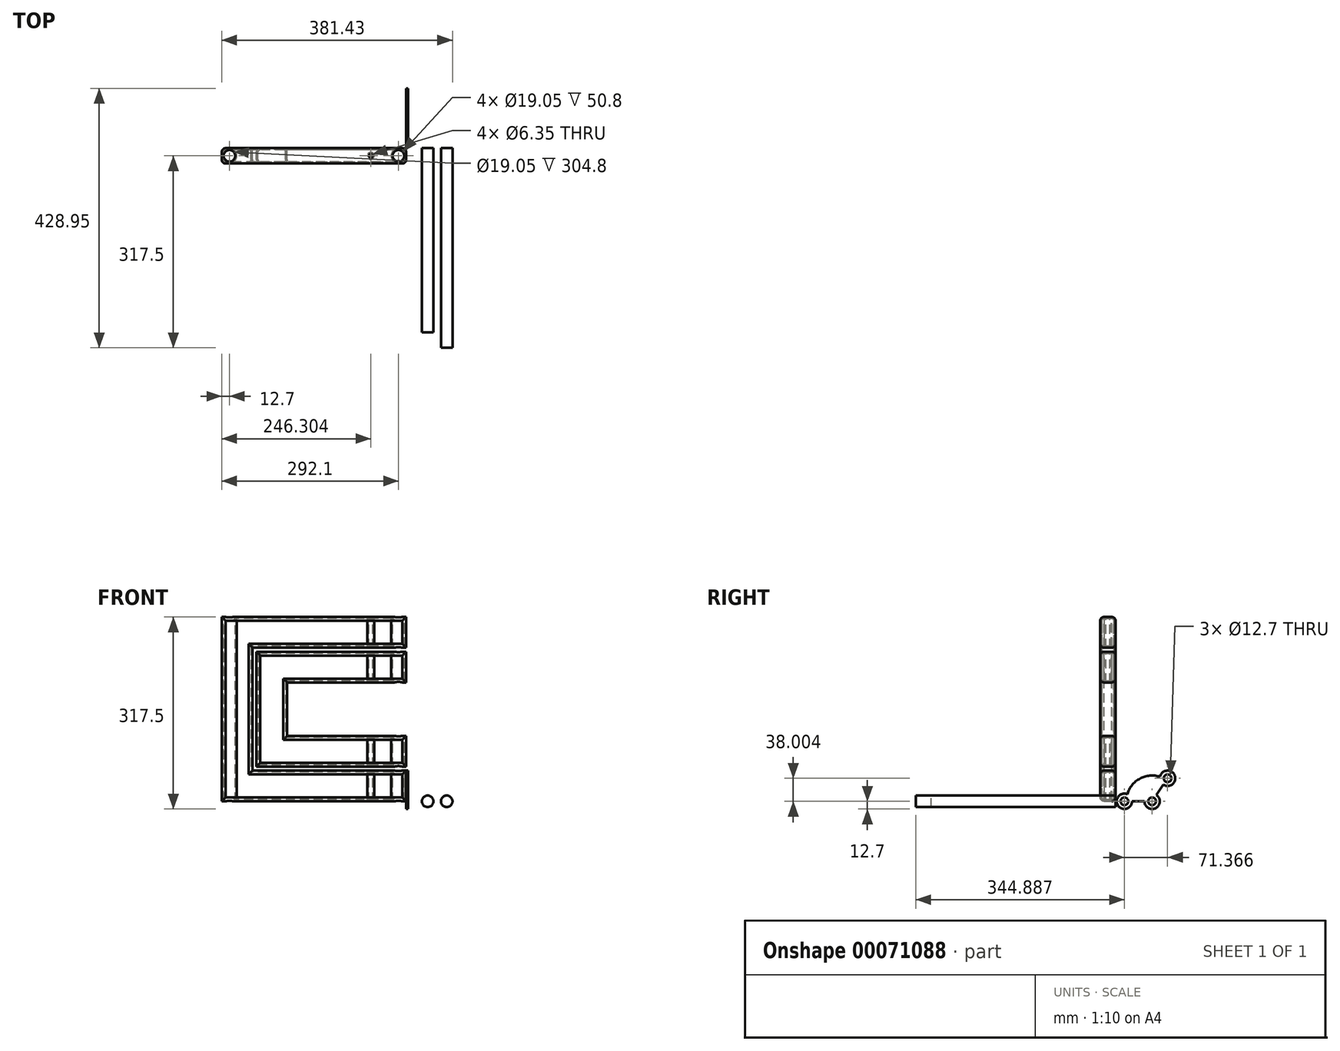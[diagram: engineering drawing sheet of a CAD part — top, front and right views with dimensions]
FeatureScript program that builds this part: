
annotation { "Feature Type Name" : "Feature", "Feature Type Description" : "" }
export const myFeature = defineFeature(function(context is Context, id is Id, definition is map)
    precondition{}
    {
        {
            var Q0;
            Q0=qCreatedBy(makeId("Front.planeOp"),FACE);
            var sketch = newSketch(context, id + "F0", { "sketchPlane" : qUnion([Q0])});
            skLineSegment(sketch, "E0.bottom", {"start": v(0, 0) * mm, "end": v(-304.8, 0) * mm});
            skLineSegment(sketch, "E0.top", {"start": v(0, 304.8) * mm, "end": v(-304.8, 304.8) * mm});
            skLineSegment(sketch, "E0.left", {"start": v(0, 0) * mm, "end": v(0, 304.8) * mm});
            skLineSegment(sketch, "E0.right", {"start": v(-304.8, 0) * mm, "end": v(-304.8, 304.8) * mm});
            skLineSegment(sketch, "E1.bottom", {"start": v(0, 254) * mm, "end": v(-254, 254) * mm});
            skLineSegment(sketch, "E1.top", {"start": v(0, 50.8) * mm, "end": v(-254, 50.8) * mm});
            skLineSegment(sketch, "E1.left", {"start": v(0, 254) * mm, "end": v(0, 50.8) * mm});
            skLineSegment(sketch, "E1.right", {"start": v(-254, 254) * mm, "end": v(-254, 50.8) * mm});
            skLineSegment(sketch, "E2.bottom", {"start": v(-253.75, 253.75) * mm, "end": v(0, 253.75) * mm});
            skLineSegment(sketch, "E2.top", {"start": v(-253.75, 51.05) * mm, "end": v(0, 51.05) * mm});
            skLineSegment(sketch, "E2.left", {"start": v(-253.75, 253.75) * mm, "end": v(-253.75, 51.05) * mm});
            skLineSegment(sketch, "E2.right", {"start": v(0, 253.75) * mm, "end": v(0, 51.05) * mm});
            skLineSegment(sketch, "E3.bottom", {"start": v(0, 196.6) * mm, "end": v(-196.6, 196.6) * mm});
            skLineSegment(sketch, "E3.top", {"start": v(0, 108.2) * mm, "end": v(-196.6, 108.2) * mm});
            skLineSegment(sketch, "E3.left", {"start": v(0, 196.6) * mm, "end": v(0, 108.2) * mm});
            skLineSegment(sketch, "E3.right", {"start": v(-196.6, 196.6) * mm, "end": v(-196.6, 108.2) * mm});
            skLineSegment(sketch, "E4.bottom", {"start": v(0, 247.4) * mm, "end": v(-247.4, 247.4) * mm});
            skLineSegment(sketch, "E4.top", {"start": v(0, 57.4) * mm, "end": v(-247.4, 57.4) * mm});
            skLineSegment(sketch, "E4.left", {"start": v(0, 247.4) * mm, "end": v(0, 57.4) * mm});
            skLineSegment(sketch, "E4.right", {"start": v(-247.4, 247.4) * mm, "end": v(-247.4, 57.4) * mm});
            skSolve(sketch);
        }
        {
            var Q0;
            {var subQ4=sQuery(id+"F0.wireOp",EDGE,"E0.bottom");Q0=makeQuery(id+"F0.imprint","IMPRINT",FACE,{"disambiguationData":[TD([[makeQuery(id+"F0.imprint","IMPRINT",EDGE,{"derivedFrom":subQ4}),-1.0]])]});}
            var Q1;
            {var subQ2=sQuery(id+"F0.wireOp",EDGE,"E3.bottom");Q1=makeQuery(id+"F0.imprint","IMPRINT",FACE,{"disambiguationData":[TD([[makeQuery(id+"F0.imprint","IMPRINT",EDGE,{"derivedFrom":subQ2}),-1.0]])]});}
            extrude(context, id + "F1", {"entities" : qUnion([Q0, Q1]), "depth" : 25.4 * mm});
        }
        {
            var Q0;
            Q0=makeQuery(id+"F1.opExtrude","SWEPT_FACE",FACE,{"disambiguationData":[OSD([sQuery(id+"F0.wireOp",EDGE,"E0.top")])]});
            var sketch = newSketch(context, id + "F2", { "sketchPlane" : qUnion([Q0])});
            skLineSegment(sketch, "E5.0", {"start": v(0, 0) * mm, "end": v(-304.8, 0) * mm});
            skLineSegment(sketch, "E5.1", {"start": v(-304.8, -25.4) * mm, "end": v(-304.8, 0) * mm});
            skLineSegment(sketch, "E5.2", {"start": v(0, -25.4) * mm, "end": v(-304.8, -25.4) * mm});
            skLineSegment(sketch, "E5.3", {"start": v(0, -25.4) * mm, "end": v(0, 0) * mm});
            skCircle(sketch, "E6", {"center": v(-292.1, -12.7) * mm, "radius": 9.53 * mm});
            skCircle(sketch, "E7", {"center": v(-12.7, -12.7) * mm, "radius": 9.53 * mm});
            skCircle(sketch, "E8", {"center": v(-241.3, -12.7) * mm, "radius": 9.53 * mm});
            skSolve(sketch);
        }
        {
            var Q0;
            Q0=makeQuery(id+"F2.imprint","IMPRINT",FACE,{"disambiguationData":[TD([[makeQuery(id+"F2.imprint","IMPRINT",EDGE,{"derivedFrom":sQuery(id+"F2.wireOp",EDGE,"E6")}),1.0]])]});
            var Q1;
            Q1=makeQuery(id+"F2.imprint","IMPRINT",FACE,{"disambiguationData":[TD([[makeQuery(id+"F2.imprint","IMPRINT",EDGE,{"derivedFrom":sQuery(id+"F2.wireOp",EDGE,"E7")}),1.0]])]});
            extrude(context, id + "F3", {"entities" : qUnion([Q0, Q1]), "operationType" : NewBodyOperationType.REMOVE, "endBound" : BoundingType.THROUGH_ALL, "oppositeDirection" : true, "depth" : 25.4 * mm});
        }
        {
            var Q0;
            Q0=qCreatedBy(makeId("Front.planeOp"),FACE);
            var sketch = newSketch(context, id + "F4", { "sketchPlane" : qUnion([Q0])});
            skCircle(sketch, "E9", {"center": v(67.1, 0) * mm, "radius": 9.52 * mm});
            skCircle(sketch, "E10", {"center": v(35.6, 0) * mm, "radius": 9.52 * mm});
            skSolve(sketch);
        }
        {
            var Q0;
            Q0=makeQuery(id+"F4.imprint","IMPRINT",FACE,{"disambiguationData":[TD([[makeQuery(id+"F4.imprint","IMPRINT",EDGE,{"derivedFrom":sQuery(id+"F4.wireOp",EDGE,"E10")}),1.0]])]});
            extrude(context, id + "F5", {"entities" : qUnion([Q0]), "depth" : 304.8 * mm});
        }
        {
            var Q0;
            Q0=makeQuery(id+"F4.imprint","IMPRINT",FACE,{"disambiguationData":[TD([[makeQuery(id+"F4.imprint","IMPRINT",EDGE,{"derivedFrom":sQuery(id+"F4.wireOp",EDGE,"E9")}),1.0]])]});
            extrude(context, id + "F6", {"entities" : qUnion([Q0]), "depth" : 330.2 * mm});
        }
        {
            var Q0;
            Q0=makeQuery(id+"F1.opExtrude","CAP_FACE",FACE,{"disambiguationData":[OSD([sQuery(id+"F0.wireOp",EDGE,"E0.bottom"),sQuery(id+"F0.wireOp",EDGE,"E0.top"),sQuery(id+"F0.wireOp",EDGE,"E0.left"),sQuery(id+"F0.wireOp",EDGE,"E0.right"),sQuery(id+"F0.wireOp",EDGE,"E1.bottom"),sQuery(id+"F0.wireOp",EDGE,"E1.top"),sQuery(id+"F0.wireOp",EDGE,"E1.right")])],"isStart":false});
            var Q1;
            Q1=makeQuery(id+"F1.opExtrude","CAP_FACE",FACE,{"disambiguationData":[OSD([sQuery(id+"F0.wireOp",EDGE,"E0.bottom"),sQuery(id+"F0.wireOp",EDGE,"E0.top"),sQuery(id+"F0.wireOp",EDGE,"E0.left"),sQuery(id+"F0.wireOp",EDGE,"E0.right"),sQuery(id+"F0.wireOp",EDGE,"E1.bottom"),sQuery(id+"F0.wireOp",EDGE,"E1.top"),sQuery(id+"F0.wireOp",EDGE,"E1.right")])],"isStart":true});
            var Q2;
            Q2=makeQuery(id+"F1.opExtrude","CAP_FACE",FACE,{"disambiguationData":[OSD([sQuery(id+"F0.wireOp",EDGE,"E2.bottom"),sQuery(id+"F0.wireOp",EDGE,"E2.top"),sQuery(id+"F0.wireOp",EDGE,"E2.left"),sQuery(id+"F0.wireOp",EDGE,"E2.right"),sQuery(id+"F0.wireOp",EDGE,"E3.bottom"),sQuery(id+"F0.wireOp",EDGE,"E3.top"),sQuery(id+"F0.wireOp",EDGE,"E3.right")])],"isStart":false});
            var Q3;
            Q3=makeQuery(id+"F1.opExtrude","CAP_FACE",FACE,{"disambiguationData":[OSD([sQuery(id+"F0.wireOp",EDGE,"E2.bottom"),sQuery(id+"F0.wireOp",EDGE,"E2.top"),sQuery(id+"F0.wireOp",EDGE,"E2.left"),sQuery(id+"F0.wireOp",EDGE,"E2.right"),sQuery(id+"F0.wireOp",EDGE,"E3.bottom"),sQuery(id+"F0.wireOp",EDGE,"E3.top"),sQuery(id+"F0.wireOp",EDGE,"E3.right")])],"isStart":true});
            fillet(context, id + "F7", {"entities" : qUnion([Q0, Q1, Q2, Q3]), "radius" : 6.35 * mm, "tangentPropagation" : true, "allowEdgeOverflow" : false});
        }
        {
            var Q0;
            Q0=qCreatedBy(makeId("Right.planeOp"),FACE);
            var sketch = newSketch(context, id + "F8", { "sketchPlane" : qUnion([Q0])});
            skCircle(sketch, "E11", {"center": v(14.69, 0) * mm, "radius": 12.7 * mm});
            skCircle(sketch, "E12", {"center": v(86.05, 38) * mm, "radius": 12.7 * mm});
            skArc(sketch, "E13.0", {"start": v(27.39, 0) * mm, "mid": v(44.93, 29.22) * mm, "end": v(78.96, 27.47) * mm});
            skArc(sketch, "E14.0", {"start": v(1.99, 0) * mm, "mid": v(33, 51.64) * mm, "end": v(93.14, 48.54) * mm});
            skArc(sketch, "E15", {"start": v(86.05, 38) * mm, "mid": v(38.96, 40.43) * mm, "end": v(14.69, 0) * mm});
            skArc(sketch, "E16.0", {"start": v(87.83, 40.64) * mm, "mid": v(37.47, 43.23) * mm, "end": v(11.51, 0) * mm});
            skArc(sketch, "E17.0", {"start": v(84.28, 35.37) * mm, "mid": v(40.45, 37.62) * mm, "end": v(17.86, 0) * mm});
            skCircle(sketch, "E18", {"center": v(86.05, 38) * mm, "radius": 6.35 * mm});
            skCircle(sketch, "E19", {"center": v(14.69, 0) * mm, "radius": 6.35 * mm});
            skCircle(sketch, "E20", {"center": v(60.49, 0) * mm, "radius": 6.35 * mm});
            skCircle(sketch, "E21", {"center": v(60.49, 0) * mm, "radius": 33.1 * mm});
            skCircle(sketch, "E22", {"center": v(60.49, 0) * mm, "radius": 12.7 * mm});
            skLineSegment(sketch, "E23", {"start": v(27.39, 0) * mm, "end": v(47.79, 0) * mm});
            skLineSegment(sketch, "E24", {"start": v(86.05, 38) * mm, "end": v(60.49, 0) * mm, "construction": true});
            skLineSegment(sketch, "E25", {"start": v(78.96, 27.47) * mm, "end": v(67.58, 10.54) * mm});
            skSolve(sketch);
        }
        {
            var Q0;
            Q0=makeQuery(id+"F7.opFillet","SPLIT",FACE,{"disambiguationData":[OD(3.0)],"derivedFrom":makeQuery(id+"F1.opExtrude","SWEPT_FACE",FACE,{"disambiguationData":[OSD([sQuery(id+"F0.wireOp",EDGE,"E0.top")])]})});
            var sketch = newSketch(context, id + "F9", { "sketchPlane" : qUnion([Q0])});
            skArc(sketch, "E26.0", {"start": v(-5.6, -6.35) * mm, "mid": v(-22.22, -12.7) * mm, "end": v(-5.6, -19.05) * mm});
            skLineSegment(sketch, "E26.1", {"start": v(-5.6, -6.35) * mm, "end": v(-5.6, -6.35) * mm});
            skArc(sketch, "E26.2", {"start": v(-5.6, -19.05) * mm, "mid": v(-3.17, -12.7) * mm, "end": v(-5.6, -6.35) * mm});
            skLineSegment(sketch, "E26.3", {"start": v(-5.6, -19.05) * mm, "end": v(-5.6, -19.05) * mm});
            skCircle(sketch, "E27", {"center": v(-58.5, -12.7) * mm, "radius": 3.18 * mm});
            skSolve(sketch);
        }
        {
            var Q0;
            {var subQ3=sQuery(id+"F8.wireOp",EDGE,"E11");var subQ5=makeQuery(id+"F8.imprint","INTERSECT",VERTEX,{"derivedFrom":[subQ3,sQuery(id+"F8.wireOp",EDGE,"E13.0")]});Q0=makeQuery(id+"F8.imprint","IMPRINT",FACE,{"disambiguationData":[TD([[makeQuery(id+"F8.imprint","IMPRINT",EDGE,{"disambiguationData":[TD([[subQ5,-1.0]])],"derivedFrom":subQ3}),1.0]])]});}
            var Q1;
            {var subQ3=sQuery(id+"F8.wireOp",EDGE,"E12");var subQ5=makeQuery(id+"F8.imprint","INTERSECT",VERTEX,{"derivedFrom":[subQ3,sQuery(id+"F8.wireOp",EDGE,"E14.0")]});Q1=makeQuery(id+"F8.imprint","IMPRINT",FACE,{"disambiguationData":[TD([[makeQuery(id+"F8.imprint","IMPRINT",EDGE,{"disambiguationData":[TD([[subQ5,-1.0]])],"derivedFrom":subQ3}),1.0]])]});}
            var Q2;
            {var subQ0=sQuery(id+"F8.wireOp",EDGE,"E13.0");Q2=makeQuery(id+"F8.imprint","IMPRINT",FACE,{"disambiguationData":[TD([[makeQuery(id+"F8.imprint","IMPRINT",EDGE,{"derivedFrom":subQ0}),1.0]])]});}
            var Q3;
            {var subQ0=sQuery(id+"F8.wireOp",EDGE,"E17.0");var subQ1=sQuery(id+"F8.wireOp",EDGE,"E11");var subQ2=makeQuery(id+"F8.imprint","INTERSECT",VERTEX,{"derivedFrom":[subQ1,subQ0]});Q3=makeQuery(id+"F8.imprint","IMPRINT",FACE,{"disambiguationData":[TD([[makeQuery(id+"F8.imprint","IMPRINT",EDGE,{"disambiguationData":[TD([[subQ2,-1.0]])],"derivedFrom":subQ1}),1.0]])]});}
            var Q4;
            {var subQ0=sQuery(id+"F8.wireOp",EDGE,"E15");var subQ1=sQuery(id+"F8.wireOp",EDGE,"E11");var subQ2=makeQuery(id+"F8.imprint","INTERSECT",VERTEX,{"derivedFrom":[subQ1,subQ0]});Q4=makeQuery(id+"F8.imprint","IMPRINT",FACE,{"disambiguationData":[TD([[makeQuery(id+"F8.imprint","IMPRINT",EDGE,{"disambiguationData":[TD([[subQ2,-1.0]])],"derivedFrom":subQ1}),1.0]])]});}
            var Q5;
            {var subQ0=sQuery(id+"F8.wireOp",EDGE,"E15");var subQ1=sQuery(id+"F8.wireOp",EDGE,"E12");var subQ2=makeQuery(id+"F8.imprint","INTERSECT",VERTEX,{"derivedFrom":[subQ1,subQ0]});Q5=makeQuery(id+"F8.imprint","IMPRINT",FACE,{"disambiguationData":[TD([[makeQuery(id+"F8.imprint","IMPRINT",EDGE,{"disambiguationData":[TD([[subQ2,-1.0]])],"derivedFrom":subQ1}),1.0]])]});}
            var Q6;
            {var subQ0=sQuery(id+"F8.wireOp",EDGE,"E16.0");var subQ1=sQuery(id+"F8.wireOp",EDGE,"E12");var subQ2=makeQuery(id+"F8.imprint","INTERSECT",VERTEX,{"derivedFrom":[subQ1,subQ0]});Q6=makeQuery(id+"F8.imprint","IMPRINT",FACE,{"disambiguationData":[TD([[makeQuery(id+"F8.imprint","IMPRINT",EDGE,{"disambiguationData":[TD([[subQ2,-1.0]])],"derivedFrom":subQ1}),1.0]])]});}
            var Q7;
            {var subQ1=sQuery(id+"F8.wireOp",EDGE,"E11");var subQ3=sQuery(id+"F8.wireOp",EDGE,"E17.0");var subQ4=makeQuery(id+"F8.imprint","INTERSECT",VERTEX,{"derivedFrom":[subQ1,subQ3]});Q7=makeQuery(id+"F8.imprint","IMPRINT",FACE,{"disambiguationData":[TD([[makeQuery(id+"F8.imprint","IMPRINT",EDGE,{"disambiguationData":[TD([[subQ4,1.0]])],"derivedFrom":subQ3}),1.0]])]});}
            var Q8;
            {var subQ0=sQuery(id+"F8.wireOp",EDGE,"E23");Q8=makeQuery(id+"F8.imprint","IMPRINT",FACE,{"disambiguationData":[TD([[makeQuery(id+"F8.imprint","IMPRINT",EDGE,{"derivedFrom":subQ0}),1.0]])]});}
            var Q9;
            Q9=makeQuery(id+"F8.imprint","IMPRINT",FACE,{"disambiguationData":[TD([[makeQuery(id+"F8.imprint","IMPRINT",EDGE,{"derivedFrom":sQuery(id+"F8.wireOp",EDGE,"E20")}),-1.0]])]});
            extrude(context, id + "F10", {"entities" : qUnion([Q0, Q1, Q2, Q3, Q4, Q5, Q6, Q7, Q8, Q9]), "depth" : 3.17 * mm});
        }
        {
            var Q0;
            Q0=makeQuery(id+"F9.imprint","IMPRINT",FACE,{"disambiguationData":[TD([[makeQuery(id+"F9.imprint","IMPRINT",EDGE,{"derivedFrom":sQuery(id+"F9.wireOp",EDGE,"E27")}),1.0]])]});
            extrude(context, id + "F11", {"entities" : qUnion([Q0]), "operationType" : NewBodyOperationType.REMOVE, "endBound" : BoundingType.THROUGH_ALL, "oppositeDirection" : true, "depth" : 25.4 * mm});
        }
        {
            var Q0;
            Q0=makeQuery(id+"F1.opExtrude","CAP_FACE",FACE,{"disambiguationData":[OSD([sQuery(id+"F0.wireOp",EDGE,"E0.bottom"),sQuery(id+"F0.wireOp",EDGE,"E0.top"),sQuery(id+"F0.wireOp",EDGE,"E0.left"),sQuery(id+"F0.wireOp",EDGE,"E0.right"),sQuery(id+"F0.wireOp",EDGE,"E1.bottom"),sQuery(id+"F0.wireOp",EDGE,"E1.top"),sQuery(id+"F0.wireOp",EDGE,"E1.right")])],"isStart":false});
            var Q1;
            Q1=makeQuery(id+"F1.opExtrude","CAP_FACE",FACE,{"disambiguationData":[OSD([sQuery(id+"F0.wireOp",EDGE,"E2.bottom"),sQuery(id+"F0.wireOp",EDGE,"E2.top"),sQuery(id+"F0.wireOp",EDGE,"E2.left"),sQuery(id+"F0.wireOp",EDGE,"E2.right"),sQuery(id+"F0.wireOp",EDGE,"E3.bottom"),sQuery(id+"F0.wireOp",EDGE,"E3.top"),sQuery(id+"F0.wireOp",EDGE,"E3.right")])],"isStart":false});
            var Q2;
            Q2=makeQuery(id+"F1.opExtrude","CAP_FACE",FACE,{"disambiguationData":[OSD([sQuery(id+"F0.wireOp",EDGE,"E0.bottom"),sQuery(id+"F0.wireOp",EDGE,"E0.top"),sQuery(id+"F0.wireOp",EDGE,"E0.left"),sQuery(id+"F0.wireOp",EDGE,"E0.right"),sQuery(id+"F0.wireOp",EDGE,"E1.bottom"),sQuery(id+"F0.wireOp",EDGE,"E1.top"),sQuery(id+"F0.wireOp",EDGE,"E1.right")])],"isStart":true});
            var Q3;
            Q3=makeQuery(id+"F1.opExtrude","CAP_FACE",FACE,{"disambiguationData":[OSD([sQuery(id+"F0.wireOp",EDGE,"E2.bottom"),sQuery(id+"F0.wireOp",EDGE,"E2.top"),sQuery(id+"F0.wireOp",EDGE,"E2.left"),sQuery(id+"F0.wireOp",EDGE,"E2.right"),sQuery(id+"F0.wireOp",EDGE,"E3.bottom"),sQuery(id+"F0.wireOp",EDGE,"E3.top"),sQuery(id+"F0.wireOp",EDGE,"E3.right")])],"isStart":true});
            shell(context, id + "F12", {"entities" : qUnion([Q0, Q1, Q2, Q3]), "thickness" : 2.54 * mm});
        }
    });
